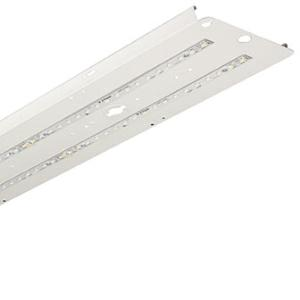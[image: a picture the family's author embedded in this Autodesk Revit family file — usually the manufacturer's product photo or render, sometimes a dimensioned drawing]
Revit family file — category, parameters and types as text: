
# Revit family: 3f_filippi_-_kit_led_retrofit_per_schermo_in_vetro_3f_filippi_-_a5148_a5185_-_kit_led_i3f_76_a3f_91_a3f__07057542446c8710
name_source: partatom
category: Lighting Fixtures
units: mm (PartAtom-declared; Revit-internal decimal feet)

## family parameters
Cut with Voids When Loaded = No
Host = Face
Light Source = No
Part Type = Normal
Room Calculation Point = No
Round Connector Dimension = Use Diameter
Shared = No

## types (1)
- 3F Filippi - Kit LED Retrofit per schermo in vetro (1 x LED, 4857 lm, 40 W, 4000 K)
    Apparent Load = 40 VA
    Approval mark = ENEC
    CIE Flux Codes = 62 90 98 100 100
    Color Rendering = 80
    Color Temperature = 4000 K
    Control Gear = Electronic ballast
    Default Elevation = 1800 mm
    Description = Led retrofit kit suitable for Fluorescent Beta 2x i3F 75, A3F 90 and A3F 92 luminaires.

ILLUMINOTECHNICAL
Luminous efficiency 100% (DLOR 100%, ULOR 0%).
Initial luminous flux of the luminaire 4857 lm.
Symmetric distribution.
Installation Interdistance Transv.D = 1.31 x hu - Long.D = 1.31 x hu.
Tabular UGR (CIE 117 - 4H-8H; S=0.25H; 70/50/20): RUG 18.5 - 19.8.
Beam angle: 90° - 99°.
Luminous efficacy 121 lm/W.
Lifetime (L93/B10): 30000 h. (tq+25°C)
Lifetime (L90/B10): 50000 h. (tq+25°C)
Lifetime (L85/B10): 80000 h. (tq+25°C)
Lifetime (L80/B10): 100000 h. (tq+25°C)
Lifetime (L85/B10): 50000 h. (tq+35°C)
Sudden decreased luminous flux after 50000 hours: 0% (C0).
Photobiological safety in compliance with IEC/TR 62778: RG0 risk exempt, (IEC 62471).
In compliance with IEC/EN 62722-2-1 - IEC/EN 62717 standards.

SOURCE
2 linear LED modules 18W/840.
Energy efficiency class (UE 2019/2020 - UE 2019/2015): D.
CIE 13.3 Colour rendering index: CRI >80 (R9 <50%).
IES TM-30 Fidelity Index: Rf = 84 Rg = 95.
CCT nominal colour temperature 4000 K.
Colour initial tolerance (MacAdam): SDCM 3.

MECHANICAL
Gear-tray unit in hot-galvanised steel, painted in white polyester, fixed to the housing by means of "Ribloc" rapid devices in galvanised steel, hinged opening.
Luminaire with limited surface temperature. - D - (EN 60598-2-24)
Dimensions: 1265x235 mm, height 105 mm. Weight 5.233 kg.
Glow-wire test resistance 850°C.

ELECTRICAL
Halogen Free electronic wiring 230V-50/60Hz, power factor 0.95, THD <25%, constant output current, SELV, class I, 1 driver.
Power of the luminaire 40 W.
CE - IEC 60598-1 - EN 60598-1.
SAFE FLICKER: PstLM=<1 and SVM=<0.4 (IEC TR 61547-1 and IEC TR 63158), to ensure a more comfortable and safe light.
Luminaire compliant with EN 60598-2-22 for power supply from a centralised emergency system CPSS (Central Power Supply System), not incorporated in the luminaire - high risk areas excluded. The default power and flux are 100% in AC and 100% in DC.
Ambient temperature from -20°C to +35°C.
Temperature class T6 max 85°C.
Relative humidity UR: <85%.

INSTALLATION
Retrofit.
Correct installation of the retrofit LED kit, compliant with EN 60598-1 and CE marked, inside the 3F Filippi - Beta 2x i3F 76, A3F 91 and A3F 93 Fluorescent luminaires must be only carried out by qualified personnel to ensure compliance with the national installation standards.
Attention: to maintain the degree of protection of the device and for the purposes of validity of the guarantee of the new retrofit kits, it is imperative to replace the old cable guides (on the body of the device) with the new ones supplied.
All accessories dedicated to this product are available on the Catalog and on our website www.3F-Filippi.com.

ACCESSORIES
A5185 - Printed glass Beta 2x i3F 76 - L1265.

WARNING
Fixture not suitable for cold stores with an ambient temperature <0°C and/or relative humidity >85%.
Luminaire designed for disposal/recycling at end-of-life.
Replaceable (LED only) light source by a professional. Replaceable control gear by a professional.
    Height = 105 mm
    Lamp = 1 x LED
    Lamp Light Flux = 4857 lm
    Lamp Power = 40 W
    Lamp count = 1
    Length = 1265 mm
    Lifetime = 50000 h
    Luminous efficacy = 121 lm/W
    Manufacturer = 3F Filippi
    ModVariant = No
    Model = 3F Filippi - A5148+A5185 - KIT LED i3F 76,A3F 91,A3F 93-L1265-2x18W + VS
    Mounting Place = Ceiling
    Mounting Type = Surface mounted
    Number of Poles = 1
    OnlyDefault = Yes
    Power Factor = 1
    Product Name = 3F Filippi - Kit LED Retrofit per schermo in vetro
    Product group = ceiling mounted luminaire
    ProductGroupID = 3
    Protection Class = Protection class I
    Protection Degree = Degree of protection
    RLX_Detail_Level = 1
    RLX_Emergency_Light_Flux = 0 lm
    RLX_Emergency_Type = 0
    RLX_Emergency_Type_DB = No
    RlxData = <blob elided: 58309 chars, md5=6be2c00f>
    Socket = socket
    Standby Power = 0 W
    System Light Flux = 4857 lm
    System Power = 40 W
    Type Comments = Product without accessories
    Type Image = 3ffilippi_a5148_a5185.jpg
    URL = http://relux.com
    VarID = ---
    Voltage = 0 V
    Weight = 0.00 kg
    Width = 235 mm

## geometry (parser evidence)
native form markers: Blend x4, Sweep x10
no freeform markers — native parametric forms only
